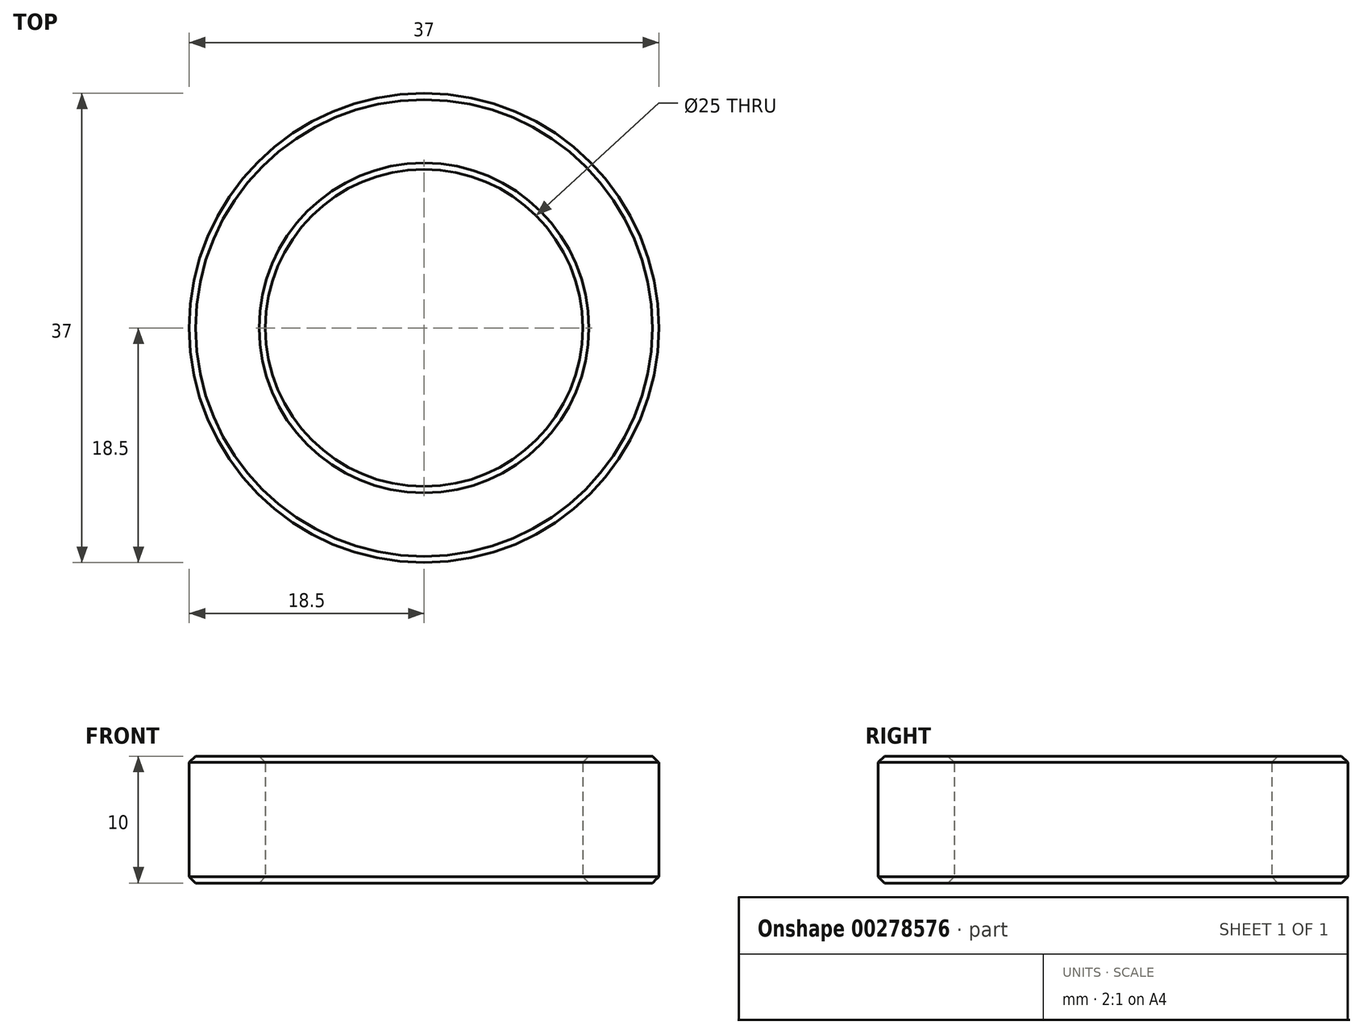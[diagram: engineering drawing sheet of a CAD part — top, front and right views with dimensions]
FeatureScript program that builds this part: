
annotation { "Feature Type Name" : "Feature", "Feature Type Description" : "" }
export const myFeature = defineFeature(function(context is Context, id is Id, definition is map)
    precondition{}
    {
        {
            var Q0;
            Q0=qCreatedBy(makeId("Top.planeOp"),FACE);
            var sketch = newSketch(context, id + "F0", { "sketchPlane" : qUnion([Q0])});
            skCircle(sketch, "E0", {"center": v(0, 0) * mm, "radius": 12.5 * mm});
            skCircle(sketch, "E1", {"center": v(0, 0) * mm, "radius": 18.5 * mm});
            skSolve(sketch);
        }
        {
            var Q0;
            Q0=makeQuery(id+"F0.imprint","IMPRINT",FACE,{"disambiguationData":[TD([[makeQuery(id+"F0.imprint","IMPRINT",EDGE,{"derivedFrom":sQuery(id+"F0.wireOp",EDGE,"E0")}),-1.0]])]});
            extrude(context, id + "F1", {"entities" : qUnion([Q0]), "depth" : 5 * mm, "hasSecondDirection" : true, "secondDirectionOppositeDirection" : true, "secondDirectionDepth" : 5 * mm});
        }
        {
            var Q0;
            Q0=makeQuery(id+"F1.opExtrude","CAP_EDGE",EDGE,{"disambiguationData":[OSD([sQuery(id+"F0.wireOp",EDGE,"E0")])],"isStart":true});
            var Q1;
            Q1=makeQuery(id+"F1.opExtrude","CAP_EDGE",EDGE,{"disambiguationData":[OSD([sQuery(id+"F0.wireOp",EDGE,"E1")])],"isStart":true});
            var Q2;
            Q2=makeQuery(id+"F1.opExtrude","CAP_EDGE",EDGE,{"disambiguationData":[OSD([sQuery(id+"F0.wireOp",EDGE,"E0")])],"isStart":false});
            var Q3;
            Q3=makeQuery(id+"F1.opExtrude","CAP_EDGE",EDGE,{"disambiguationData":[OSD([sQuery(id+"F0.wireOp",EDGE,"E1")])],"isStart":false});
            chamfer(context, id + "F2", {"entities" : qUnion([Q0, Q1, Q2, Q3]), "width" : 0.5 * mm, "tangentPropagation" : true});
        }
    });
